# Revit family: Lighting_Outside_L-L-Luce-Light_Plin-3
name_source: partatom
category: Lighting Fixtures
units: mm (PartAtom-declared; Revit-internal decimal feet)

## family parameters
Always vertical = No
Cut with Voids When Loaded = No
Light Source = No
OmniClass Number = 23.80.70.00
OmniClass Title = Lighting
Part Type = Normal
Room Calculation Point = No
Round Connector Dimension = Use Diameter
Shared = No
Work Plane-Based = Yes

## types (3) — shared parameters
Body = Head and column in aluminium
Default Elevation = 1219 mm
Installation instructions = https://www.lucelight.it
Luce-Light_Applications = floor
Luce-Light_Body_material = screen in serigraphed, tempered extraclear glass
Luce-Light_Classification = CE
Luce-Light_Color_Rendering_Index_CRI = 80
Luce-Light_Finishes_material = grey, anthracite, cor-ten, white
Luce-Light_IK = 08
Luce-Light_IP = 65
Luce-Light_LED_colour = 2700K, 3000K, 4000K
Luce-Light_LED_light_sources = 36 mid power LEDs, 3-step MacAdam, 50 000h L85 B10 (Ta 25°C)
Luce-Light_Mounting = surface mounted
Luce-Light_Note = Non-standard heights available on request
Luce-Light_Optical_assembly = diffuse, asymmetrical
Luce-Light_Power = 24W
Luce-Light_Power_Class = 230Vac
Luce-Light_Screen_material = glass
Luce-Light_Total_flow_rate = 492 lm (3000K) per beam
Luce-Light_lumen-output-at-source = 1242 lm (3000K) per beam
Manufacturer = L&L Luce&Light
Material = Metal-Luce&Light-Aluminium
Nominal height = 560 mm
Nominal width = 124 mm
Product Guid = 4741dd45-82ca-4056-b86c-70add1bd27d8
Product data url = https://www.bimobject.com
Product url = https://www.lucelight.it
Secondary material = Screen in glass
Technical description = https://www.lucelight.it
URL = https://www.lucelight.it
Wattage Comments = 24W
zero-valued in all types: PLIN 3.1 A 3000K 24W 230Vac h560 - White

## per-type parameters (varying)
| type | Light type |
| PLIN 3.1 A 4000K 24W 230Vac h560 | Family2 : PLIN 3.1 A 4000K 24W 230Vac h560 |
| PLIN 3.1 A 2700K 24W 230Vac h560 | Family2 : PLIN 3.1 A 2700K 24W 230Vac h560 |
| PLIN 3.1 A 3000K 24W 230Vac h560 | Family2 : PLIN 3.1 A 3000K 24W 230Vac h560 |

## geometry (parser evidence)
native form markers: Sweep x6
no freeform markers — native parametric forms only
